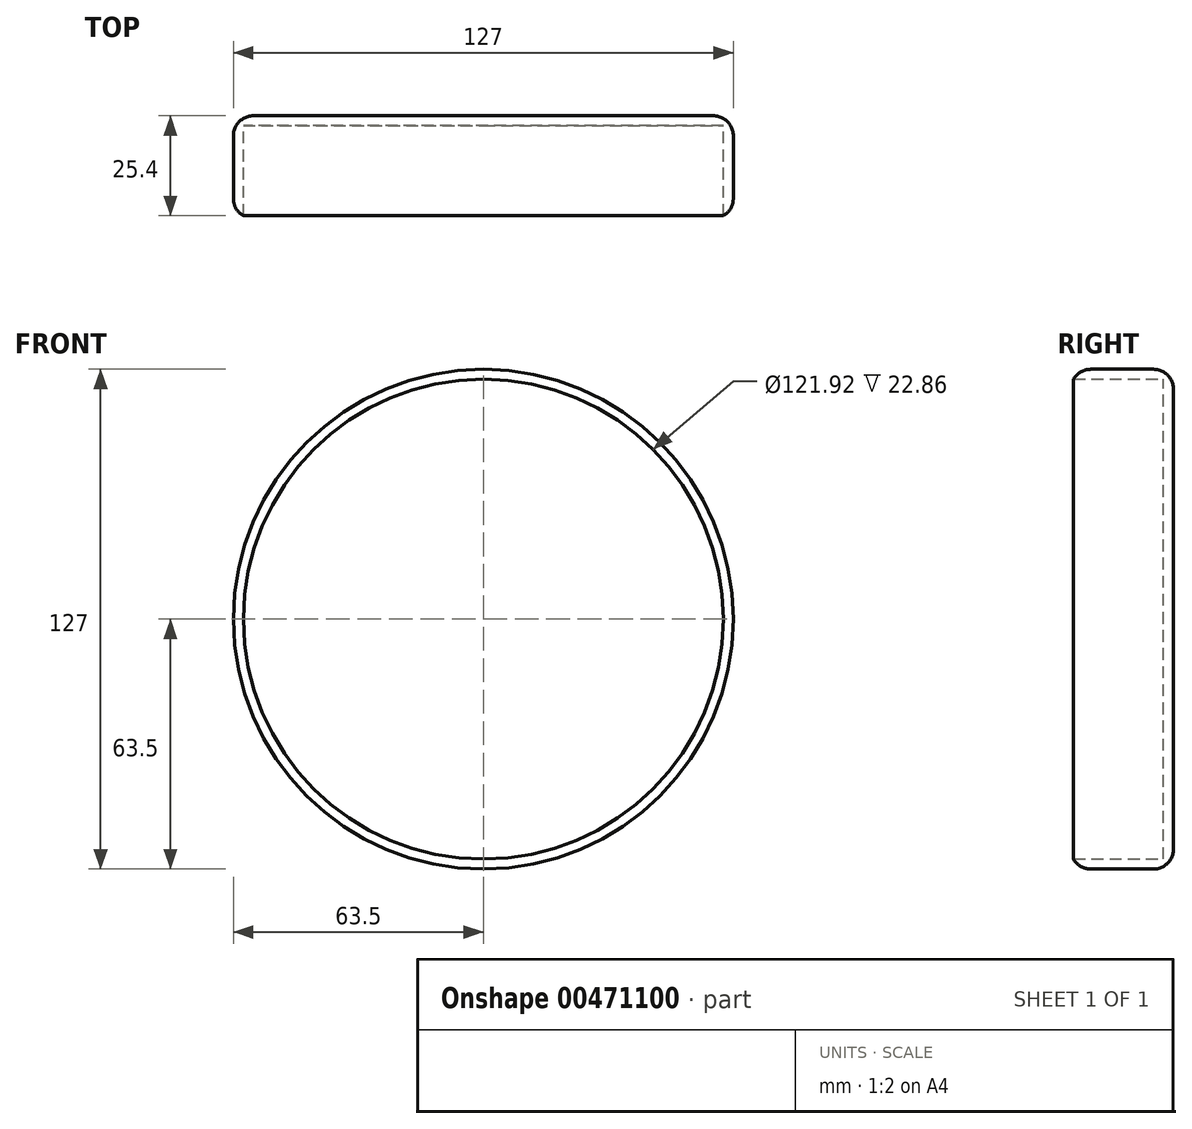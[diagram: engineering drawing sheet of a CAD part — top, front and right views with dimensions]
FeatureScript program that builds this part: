
annotation { "Feature Type Name" : "Feature", "Feature Type Description" : "" }
export const myFeature = defineFeature(function(context is Context, id is Id, definition is map)
    precondition{}
    {
        {
            var Q0;
            Q0=qCreatedBy(makeId("Front.planeOp"),FACE);
            var sketch = newSketch(context, id + "F0", { "sketchPlane" : qUnion([Q0])});
            skCircle(sketch, "E0", {"center": v(0, 0) * mm, "radius": 63.5 * mm});
            skSolve(sketch);
        }
        {
            var Q0;
            Q0=makeQuery(id+"F0.imprint","IMPRINT",FACE,{"disambiguationData":[TD([[makeQuery(id+"F0.imprint","IMPRINT",EDGE,{"derivedFrom":sQuery(id+"F0.wireOp",EDGE,"E0")}),1.0]])]});
            extrude(context, id + "F1", {"entities" : qUnion([Q0]), "depth" : 25.4 * mm});
        }
        {
            var Q0;
            Q0=makeQuery(id+"F1.opExtrude","CAP_FACE",FACE,{"disambiguationData":[OSD([sQuery(id+"F0.wireOp",EDGE,"E0")])],"isStart":false});
            shell(context, id + "F2", {"entities" : qUnion([Q0]), "thickness" : 2.54 * mm});
        }
        {
            var Q0;
            Q0=makeQuery(id+"F1.opExtrude","SWEPT_FACE",FACE,{"disambiguationData":[OSD([sQuery(id+"F0.wireOp",EDGE,"E0")])]});
            fillet(context, id + "F3", {"entities" : qUnion([Q0]), "radius" : 5.08 * mm, "tangentPropagation" : true, "allowEdgeOverflow" : false});
        }
    });
